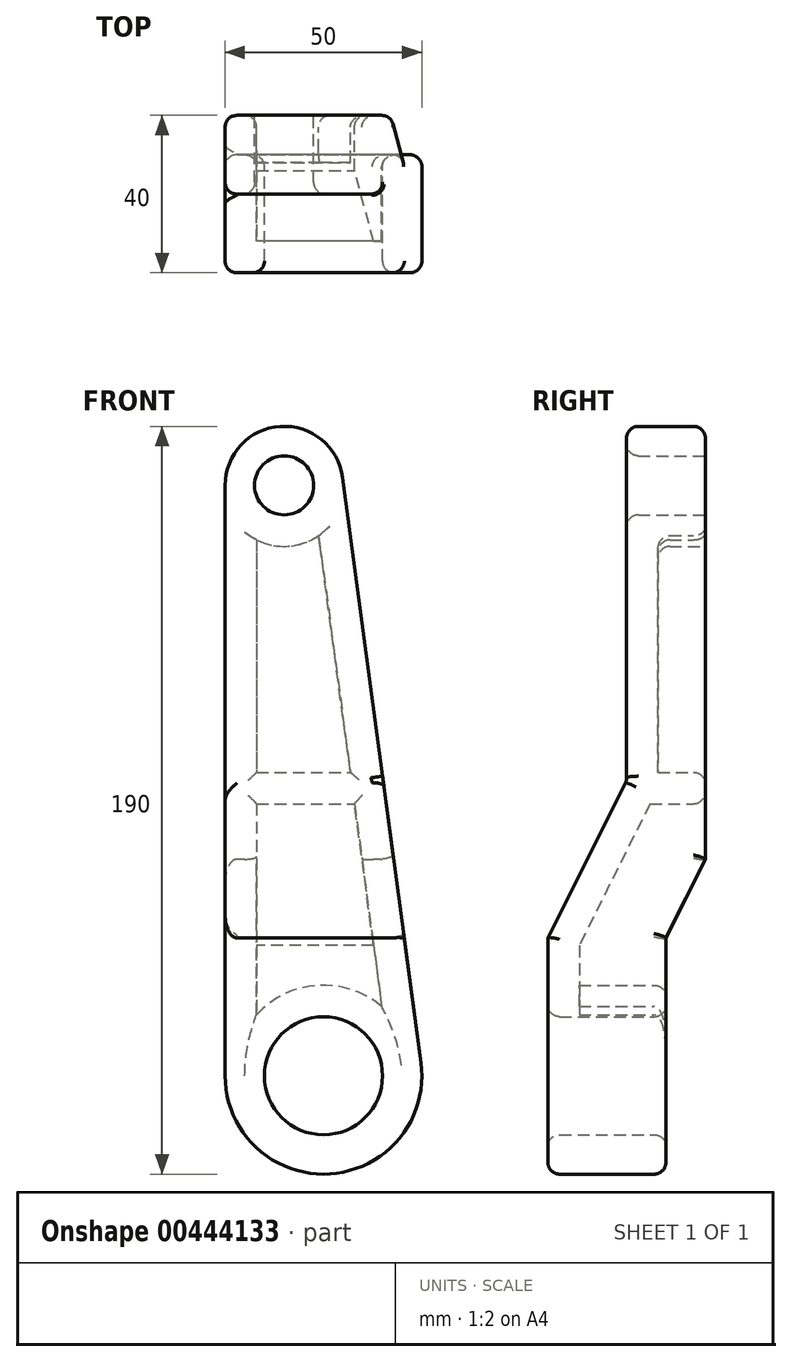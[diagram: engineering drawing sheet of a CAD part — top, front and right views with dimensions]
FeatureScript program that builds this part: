
annotation { "Feature Type Name" : "Feature", "Feature Type Description" : "" }
export const myFeature = defineFeature(function(context is Context, id is Id, definition is map)
    precondition{}
    {
        {
            var Q0;
            Q0=qCreatedBy(makeId("Front.planeOp"),FACE);
            var sketch = newSketch(context, id + "F0", { "sketchPlane" : qUnion([Q0])});
            skArc(sketch, "E0", {"start": v(-25, 0) * mm, "mid": v(1.66, -24.94) * mm, "end": v(24.78, 3.32) * mm});
            skArc(sketch, "E1", {"start": v(4.87, 152) * mm, "mid": v(-11, 164.97) * mm, "end": v(-25, 150) * mm});
            skLineSegment(sketch, "E2", {"start": v(-25, 150) * mm, "end": v(-25, 0) * mm});
            skLineSegment(sketch, "E3", {"start": v(4.87, 152) * mm, "end": v(24.78, 3.32) * mm});
            skPoint(sketch, "E4.orphan", {"position": v(0, 188.33) * mm});
            skSolve(sketch);
        }
        {
            var Q0;
            Q0 = qSketchRegion(id + "F0", true);
            extrude(context, id + "F1", {"entities" : qUnion([Q0]), "depth" : 40 * mm});
        }
        {
            var Q0;
            Q0=makeQuery(id+"F1.opExtrude","SWEPT_FACE",FACE,{"disambiguationData":[OSD([sQuery(id+"F0.wireOp",EDGE,"E2")])]});
            var sketch = newSketch(context, id + "F2", { "sketchPlane" : qUnion([Q0])});
            skLineSegment(sketch, "E5", {"start": v(0, 55) * mm, "end": v(0, -25.94) * mm});
            skLineSegment(sketch, "E6", {"start": v(10, -25.94) * mm, "end": v(10, 35) * mm});
            skLineSegment(sketch, "E7", {"start": v(10, 35) * mm, "end": v(0, 55) * mm});
            skLineSegment(sketch, "E8", {"start": v(40, 35) * mm, "end": v(40, 165.97) * mm});
            skLineSegment(sketch, "E9", {"start": v(20, 165.97) * mm, "end": v(20, 75) * mm});
            skLineSegment(sketch, "E10", {"start": v(20, 75) * mm, "end": v(40, 35) * mm});
            skLineSegment(sketch, "E11", {"start": v(0, -25.94) * mm, "end": v(10, -25.94) * mm});
            skLineSegment(sketch, "E12", {"start": v(20, 165.97) * mm, "end": v(40, 165.97) * mm});
            skSolve(sketch);
        }
        {
            var Q0;
            Q0 = qSketchRegion(id + "F2", true);
            extrude(context, id + "F3", {"entities" : qUnion([Q0]), "operationType" : NewBodyOperationType.REMOVE, "endBound" : BoundingType.THROUGH_ALL, "oppositeDirection" : true, "depth" : 25 * mm});
        }
        {
            var Q0;
            Q0=makeQuery(id+"F1.opExtrude","CAP_FACE",FACE,{"disambiguationData":[OSD([sQuery(id+"F0.wireOp",EDGE,"E0"),sQuery(id+"F0.wireOp",EDGE,"E1"),sQuery(id+"F0.wireOp",EDGE,"E2"),sQuery(id+"F0.wireOp",EDGE,"E3")])],"isStart":true});
            var sketch = newSketch(context, id + "F4", { "sketchPlane" : qUnion([Q0])});
            skCircle(sketch, "E13", {"center": v(10, 150) * mm, "radius": 7.5 * mm});
            skCircle(sketch, "E14", {"center": v(0, 0) * mm, "radius": 15 * mm});
            skSolve(sketch);
        }
        {
            var Q0;
            Q0 = qSketchRegion(id + "F4", true);
            extrude(context, id + "F5", {"entities" : qUnion([Q0]), "operationType" : NewBodyOperationType.REMOVE, "endBound" : BoundingType.THROUGH_ALL, "oppositeDirection" : true, "depth" : 25 * mm});
        }
        {
            var Q0;
            Q0=makeQuery(id+"F1.opExtrude","CAP_FACE",FACE,{"disambiguationData":[OSD([sQuery(id+"F0.wireOp",EDGE,"E0"),sQuery(id+"F0.wireOp",EDGE,"E1"),sQuery(id+"F0.wireOp",EDGE,"E2"),sQuery(id+"F0.wireOp",EDGE,"E3")])],"isStart":true});
            var Q1;
            Q1=makeQuery(id+"F3.boolean.opBoolean","COPY",FACE,{"derivedFrom":makeQuery(id+"F3.opExtrude","SWEPT_FACE",FACE,{"disambiguationData":[OSD([sQuery(id+"F2.wireOp",EDGE,"E7")])]})});
            var Q2;
            Q2=makeQuery(id+"F3.boolean.opBoolean","COPY",FACE,{"derivedFrom":makeQuery(id+"F3.opExtrude","SWEPT_FACE",FACE,{"disambiguationData":[OSD([sQuery(id+"F2.wireOp",EDGE,"E6")])]})});
            shell(context, id + "F6", {"entities" : qUnion([Q0, Q1, Q2]), "thickness" : 8 * mm});
        }
        {
            var Q0;
            Q0=makeQuery(id+"F1.opExtrude","CAP_FACE",FACE,{"disambiguationData":[OSD([sQuery(id+"F0.wireOp",EDGE,"E0"),sQuery(id+"F0.wireOp",EDGE,"E1"),sQuery(id+"F0.wireOp",EDGE,"E2"),sQuery(id+"F0.wireOp",EDGE,"E3")])],"isStart":true});
            var sketch = newSketch(context, id + "F7", { "sketchPlane" : qUnion([Q0])});
            skLineSegment(sketch, "E15", {"start": v(-6.82, 77.11) * mm, "end": v(17, 77.11) * mm});
            skLineSegment(sketch, "E16", {"start": v(-7.9, 69.11) * mm, "end": v(17, 69.11) * mm});
            skLineSegment(sketch, "E17.0", {"start": v(-6.82, 77.11) * mm, "end": v(-7.9, 69.11) * mm});
            skLineSegment(sketch, "E18.0", {"start": v(17, 77.11) * mm, "end": v(17, 69.11) * mm});
            skPoint(sketch, "E19.orphan", {"position": v(1.23, 137.22) * mm});
            skPoint(sketch, "E20.orphan", {"position": v(17, 136.17) * mm});
            skPoint(sketch, "E21.orphan", {"position": v(-9.79, 55) * mm});
            skPoint(sketch, "E22.orphan", {"position": v(17, 55) * mm});
            skSolve(sketch);
        }
        {
            var Q0;
            Q0 = qSketchRegion(id + "F7", true);
            extrude(context, id + "F8", {"entities" : qUnion([Q0]), "operationType" : NewBodyOperationType.ADD, "endBound" : BoundingType.UP_TO_NEXT, "oppositeDirection" : true, "depth" : 25 * mm});
        }
        {
            var Q0;
            Q0=makeQuery(id+"F1.opExtrude","CAP_EDGE",EDGE,{"disambiguationData":[OSD([sQuery(id+"F0.wireOp",EDGE,"E1")])],"isStart":true});
            var Q1;
            Q1=makeQuery(id+"F5.boolean.opBoolean","COPY",EDGE,{"derivedFrom":makeQuery(id+"F5.opExtrude","CAP_EDGE",EDGE,{"disambiguationData":[OSD([sQuery(id+"F4.wireOp",EDGE,"E13")])],"isStart":true})});
            var Q2;
            Q2=makeQuery(id+"F3.boolean.opBoolean","INTERSECT",EDGE,{"derivedFrom":[makeQuery(id+"F1.opExtrude","SWEPT_FACE",FACE,{"disambiguationData":[OSD([sQuery(id+"F0.wireOp",EDGE,"E3")])]}),makeQuery(id+"F3.opExtrude","SWEPT_FACE",FACE,{"disambiguationData":[OSD([sQuery(id+"F2.wireOp",EDGE,"E10")])]})]});
            var Q3;
            Q3=makeQuery(id+"F3.boolean.opBoolean","INTERSECT",EDGE,{"derivedFrom":[makeQuery(id+"F1.opExtrude","SWEPT_FACE",FACE,{"disambiguationData":[OSD([sQuery(id+"F0.wireOp",EDGE,"E3")])]}),makeQuery(id+"F3.opExtrude","SWEPT_FACE",FACE,{"disambiguationData":[OSD([sQuery(id+"F2.wireOp",EDGE,"E9")])]})]});
            var Q4;
            {var subQ1=sQuery(id+"F0.wireOp",EDGE,"E3");Q4=makeQuery(id+"F8.boolean.opBoolean","SPLIT",EDGE,{"disambiguationData":[TD([makeQuery(id+"F6.opShell","OFFSET_FACE",FACE,{"disambiguationData":[OSD([sQuery(id+"F4.wireOp",EDGE,"E13")])]})])],"derivedFrom":makeQuery(id+"F6.opShell","OFFSET_EDGE",EDGE,{"disambiguationData":[OSD([subQ1]),TDD([makeQuery(id+"F1.opExtrude","CAP_EDGE",EDGE,{"disambiguationData":[OSD([subQ1])],"isStart":true})])]})});}
            var Q5;
            {var subQ1=sQuery(id+"F0.wireOp",EDGE,"E2");Q5=makeQuery(id+"F8.boolean.opBoolean","SPLIT",EDGE,{"disambiguationData":[TD([makeQuery(id+"F6.opShell","OFFSET_FACE",FACE,{"disambiguationData":[OSD([sQuery(id+"F4.wireOp",EDGE,"E13")])]})])],"derivedFrom":makeQuery(id+"F6.opShell","OFFSET_EDGE",EDGE,{"disambiguationData":[OSD([subQ1]),TDD([makeQuery(id+"F1.opExtrude","CAP_EDGE",EDGE,{"disambiguationData":[OSD([subQ1])],"isStart":true})])]})});}
            var Q6;
            Q6=makeQuery(id+"F1.opExtrude","CAP_EDGE",EDGE,{"disambiguationData":[OSD([sQuery(id+"F0.wireOp",EDGE,"E2")])],"isStart":true});
            var Q7;
            Q7=makeQuery(id+"F1.opExtrude","CAP_EDGE",EDGE,{"disambiguationData":[OSD([sQuery(id+"F0.wireOp",EDGE,"E3")])],"isStart":true});
            var Q8;
            Q8=makeQuery(id+"F6.opShell","OFFSET_EDGE",EDGE,{"disambiguationData":[OSD([sQuery(id+"F4.wireOp",EDGE,"E13")])]});
            var Q9;
            Q9=makeQuery(id+"F8.opExtrude","CAP_EDGE",EDGE,{"disambiguationData":[OSD([sQuery(id+"F7.wireOp",EDGE,"E16")])],"isStart":true});
            var Q10;
            {var subQ1=sQuery(id+"F0.wireOp",EDGE,"E3");Q10=makeQuery(id+"F8.boolean.opBoolean","SPLIT",EDGE,{"disambiguationData":[TD([makeQuery(id+"F6.opShell","OFFSET_FACE",FACE,{"disambiguationData":[OSD([sQuery(id+"F2.wireOp",EDGE,"E7")])]})])],"derivedFrom":makeQuery(id+"F6.opShell","OFFSET_EDGE",EDGE,{"disambiguationData":[OSD([subQ1]),TDD([makeQuery(id+"F1.opExtrude","CAP_EDGE",EDGE,{"disambiguationData":[OSD([subQ1])],"isStart":true})])]})});}
            var Q11;
            Q11=makeQuery(id+"F6.opShell","OFFSET_EDGE",EDGE,{"disambiguationData":[OSD([sQuery(id+"F0.wireOp",EDGE,"E3"),sQuery(id+"F2.wireOp",EDGE,"E7")])]});
            var Q12;
            Q12=makeQuery(id+"F6.opShell","OFFSET_EDGE",EDGE,{"disambiguationData":[OSD([sQuery(id+"F0.wireOp",EDGE,"E3"),sQuery(id+"F2.wireOp",EDGE,"E6")])]});
            var Q13;
            Q13=makeQuery(id+"F6.opShell","OFFSET_EDGE",EDGE,{"disambiguationData":[OSD([sQuery(id+"F2.wireOp",EDGE,"E6"),sQuery(id+"F4.wireOp",EDGE,"E14")])]});
            var Q14;
            Q14=makeQuery(id+"F5.boolean.opBoolean","INTERSECT",EDGE,{"derivedFrom":[makeQuery(id+"F3.boolean.opBoolean","COPY",FACE,{"derivedFrom":makeQuery(id+"F3.opExtrude","SWEPT_FACE",FACE,{"disambiguationData":[OSD([sQuery(id+"F2.wireOp",EDGE,"E6")])]})}),makeQuery(id+"F5.opExtrude","SWEPT_FACE",FACE,{"disambiguationData":[OSD([sQuery(id+"F4.wireOp",EDGE,"E14")])]})]});
            var Q15;
            Q15=makeQuery(id+"F3.boolean.opBoolean","INTERSECT",EDGE,{"derivedFrom":[makeQuery(id+"F1.opExtrude","SWEPT_FACE",FACE,{"disambiguationData":[OSD([sQuery(id+"F0.wireOp",EDGE,"E3")])]}),makeQuery(id+"F3.opExtrude","SWEPT_FACE",FACE,{"disambiguationData":[OSD([sQuery(id+"F2.wireOp",EDGE,"E7")])]})]});
            var Q16;
            Q16=makeQuery(id+"F3.boolean.opBoolean","INTERSECT",EDGE,{"derivedFrom":[makeQuery(id+"F1.opExtrude","SWEPT_FACE",FACE,{"disambiguationData":[OSD([sQuery(id+"F0.wireOp",EDGE,"E3")])]}),makeQuery(id+"F3.opExtrude","SWEPT_FACE",FACE,{"disambiguationData":[OSD([sQuery(id+"F2.wireOp",EDGE,"E6")])]})]});
            var Q17;
            Q17=makeQuery(id+"F6.opShell","OFFSET_EDGE",EDGE,{"disambiguationData":[OSD([sQuery(id+"F2.wireOp",EDGE,"E7")])]});
            var Q18;
            {var subQ0=sQuery(id+"F0.wireOp",EDGE,"E2");Q18=makeQuery(id+"F8.boolean.opBoolean","SPLIT",EDGE,{"disambiguationData":[TD([makeQuery(id+"F3.boolean.opBoolean","COPY",FACE,{"derivedFrom":makeQuery(id+"F3.opExtrude","SWEPT_FACE",FACE,{"disambiguationData":[OSD([sQuery(id+"F2.wireOp",EDGE,"E7")])]})})])],"derivedFrom":makeQuery(id+"F6.opShell","OFFSET_EDGE",EDGE,{"disambiguationData":[OSD([subQ0]),TDD([makeQuery(id+"F1.opExtrude","CAP_EDGE",EDGE,{"disambiguationData":[OSD([subQ0])],"isStart":true})])]})});}
            var Q19;
            Q19=makeQuery(id+"F3.boolean.opBoolean","COPY",EDGE,{"derivedFrom":makeQuery(id+"F3.opExtrude","CAP_EDGE",EDGE,{"disambiguationData":[OSD([sQuery(id+"F2.wireOp",EDGE,"E7")])],"isStart":true})});
            var Q20;
            Q20=makeQuery(id+"F3.boolean.opBoolean","INTERSECT",EDGE,{"derivedFrom":[makeQuery(id+"F1.opExtrude","SWEPT_FACE",FACE,{"disambiguationData":[OSD([sQuery(id+"F0.wireOp",EDGE,"E1")])]}),makeQuery(id+"F3.opExtrude","SWEPT_FACE",FACE,{"disambiguationData":[OSD([sQuery(id+"F2.wireOp",EDGE,"E9")])]})]});
            var Q21;
            Q21=makeQuery(id+"F5.boolean.opBoolean","INTERSECT",EDGE,{"derivedFrom":[makeQuery(id+"F3.boolean.opBoolean","COPY",FACE,{"derivedFrom":makeQuery(id+"F3.opExtrude","SWEPT_FACE",FACE,{"disambiguationData":[OSD([sQuery(id+"F2.wireOp",EDGE,"E9")])]})}),makeQuery(id+"F5.opExtrude","SWEPT_FACE",FACE,{"disambiguationData":[OSD([sQuery(id+"F4.wireOp",EDGE,"E13")])]})]});
            var Q22;
            Q22=makeQuery(id+"F3.boolean.opBoolean","COPY",EDGE,{"derivedFrom":makeQuery(id+"F3.opExtrude","CAP_EDGE",EDGE,{"disambiguationData":[OSD([sQuery(id+"F2.wireOp",EDGE,"E9")])],"isStart":true})});
            var Q23;
            Q23=makeQuery(id+"F3.boolean.opBoolean","COPY",EDGE,{"derivedFrom":makeQuery(id+"F3.opExtrude","CAP_EDGE",EDGE,{"disambiguationData":[OSD([sQuery(id+"F2.wireOp",EDGE,"E10")])],"isStart":true})});
            var Q24;
            Q24=makeQuery(id+"F3.boolean.opBoolean","COPY",EDGE,{"derivedFrom":makeQuery(id+"F3.opExtrude","SWEPT_EDGE",EDGE,{"disambiguationData":[OSD([sQuery(id+"F2.wireOp",EDGE,"E9"),sQuery(id+"F2.wireOp",EDGE,"E10")])]})});
            var Q25;
            Q25=makeQuery(id+"F3.boolean.opBoolean","COPY",EDGE,{"derivedFrom":makeQuery(id+"F3.opExtrude","SWEPT_EDGE",EDGE,{"disambiguationData":[OSD([sQuery(id+"F0.wireOp",EDGE,"E2"),sQuery(id+"F2.wireOp",EDGE,"E8"),sQuery(id+"F2.wireOp",EDGE,"E10")])]})});
            var Q26;
            Q26=makeQuery(id+"F1.opExtrude","CAP_EDGE",EDGE,{"disambiguationData":[OSD([sQuery(id+"F0.wireOp",EDGE,"E2")])],"isStart":false});
            var Q27;
            Q27=makeQuery(id+"F1.opExtrude","CAP_EDGE",EDGE,{"disambiguationData":[OSD([sQuery(id+"F0.wireOp",EDGE,"E3")])],"isStart":false});
            var Q28;
            Q28=makeQuery(id+"F1.opExtrude","CAP_EDGE",EDGE,{"disambiguationData":[OSD([sQuery(id+"F0.wireOp",EDGE,"E0")])],"isStart":false});
            var Q29;
            Q29=makeQuery(id+"F5.boolean.opBoolean","INTERSECT",EDGE,{"derivedFrom":[makeQuery(id+"F1.opExtrude","CAP_FACE",FACE,{"disambiguationData":[OSD([sQuery(id+"F0.wireOp",EDGE,"E0"),sQuery(id+"F0.wireOp",EDGE,"E1"),sQuery(id+"F0.wireOp",EDGE,"E2"),sQuery(id+"F0.wireOp",EDGE,"E3")])],"isStart":false}),makeQuery(id+"F5.opExtrude","SWEPT_FACE",FACE,{"disambiguationData":[OSD([sQuery(id+"F4.wireOp",EDGE,"E14")])]})]});
            var Q30;
            Q30=makeQuery(id+"F3.boolean.opBoolean","COPY",EDGE,{"derivedFrom":makeQuery(id+"F3.opExtrude","CAP_EDGE",EDGE,{"disambiguationData":[OSD([sQuery(id+"F2.wireOp",EDGE,"E6")])],"isStart":true})});
            var Q31;
            Q31=makeQuery(id+"F3.boolean.opBoolean","INTERSECT",EDGE,{"derivedFrom":[makeQuery(id+"F1.opExtrude","SWEPT_FACE",FACE,{"disambiguationData":[OSD([sQuery(id+"F0.wireOp",EDGE,"E0")])]}),makeQuery(id+"F3.opExtrude","SWEPT_FACE",FACE,{"disambiguationData":[OSD([sQuery(id+"F2.wireOp",EDGE,"E6")])]})]});
            var Q32;
            Q32=makeQuery(id+"F8.opExtrude","CAP_EDGE",EDGE,{"disambiguationData":[OSD([sQuery(id+"F7.wireOp",EDGE,"E15")])],"isStart":true});
            var Q33;
            Q33=makeQuery(id+"F6.opShell","OFFSET_EDGE",EDGE,{"disambiguationData":[OSD([sQuery(id+"F2.wireOp",EDGE,"E6")])]});
            fillet(context, id + "F9", {"entities" : qUnion([Q0, Q1, Q2, Q3, Q4, Q5, Q6, Q7, Q8, Q9, Q10, Q11, Q12, Q13, Q14, Q15, Q16, Q17, Q18, Q19, Q20, Q21, Q22, Q23, Q24, Q25, Q26, Q27, Q28, Q29, Q30, Q31, Q32, Q33]), "radius" : 3 * mm, "tangentPropagation" : true, "allowEdgeOverflow" : false});
        }
    });
